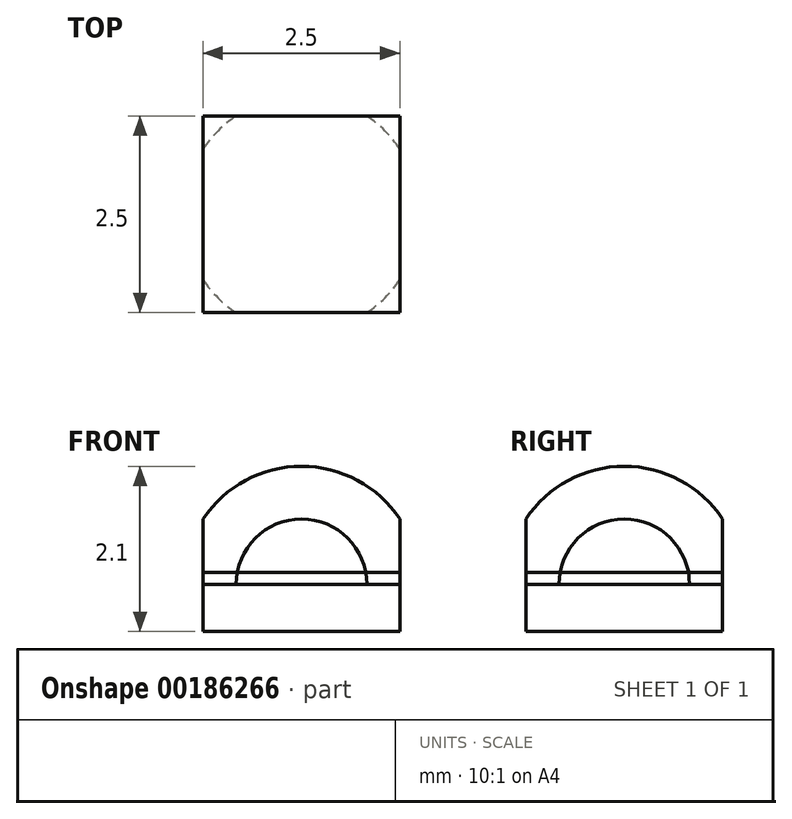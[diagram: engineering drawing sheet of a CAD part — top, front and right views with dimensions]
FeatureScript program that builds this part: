
annotation { "Feature Type Name" : "Feature", "Feature Type Description" : "" }
export const myFeature = defineFeature(function(context is Context, id is Id, definition is map)
    precondition{}
    {
        {
            var Q0;
            Q0=qCreatedBy(makeId("Top.planeOp"),FACE);
            var sketch = newSketch(context, id + "F0", { "sketchPlane" : qUnion([Q0])});
            skLineSegment(sketch, "E0.bottom", {"start": v(1.25, 1.25) * mm, "end": v(-1.25, 1.25) * mm});
            skLineSegment(sketch, "E0.top", {"start": v(1.25, -1.25) * mm, "end": v(-1.25, -1.25) * mm});
            skLineSegment(sketch, "E0.left", {"start": v(1.25, 1.25) * mm, "end": v(1.25, -1.25) * mm});
            skLineSegment(sketch, "E0.right", {"start": v(-1.25, 1.25) * mm, "end": v(-1.25, -1.25) * mm});
            skPoint(sketch, "E0.middle", {"position": v(0, 0) * mm});
            skSolve(sketch);
        }
        {
            var Q0;
            Q0 = qSketchRegion(id + "F0", true);
            extrude(context, id + "F1", {"entities" : qUnion([Q0]), "depth" : .6 * mm});
        }
        {
            var Q0;
            Q0=makeQuery(id+"F1.opExtrude","CAP_FACE",FACE,{"disambiguationData":[OSD([sQuery(id+"F0.wireOp",EDGE,"E0.bottom"),sQuery(id+"F0.wireOp",EDGE,"E0.top"),sQuery(id+"F0.wireOp",EDGE,"E0.left"),sQuery(id+"F0.wireOp",EDGE,"E0.right")])],"isStart":false});
            var sketch = newSketch(context, id + "F2", { "sketchPlane" : qUnion([Q0])});
            skLineSegment(sketch, "E1.bottom", {"start": v(-1.25, -1.25) * mm, "end": v(1.25, -1.25) * mm});
            skLineSegment(sketch, "E1.top", {"start": v(-1.25, 1.25) * mm, "end": v(1.25, 1.25) * mm});
            skLineSegment(sketch, "E1.left", {"start": v(-1.25, -1.25) * mm, "end": v(-1.25, 1.25) * mm});
            skLineSegment(sketch, "E1.right", {"start": v(1.25, -1.25) * mm, "end": v(1.25, 1.25) * mm});
            skSolve(sketch);
        }
        {
            var Q0;
            Q0 = qSketchRegion(id + "F2", true);
            extrude(context, id + "F3", {"entities" : qUnion([Q0]), "depth" : .15 * mm});
        }
        {
            var Q0;
            Q0=qCreatedBy(makeId("Front.planeOp"),FACE);
            var sketch = newSketch(context, id + "F4", { "sketchPlane" : qUnion([Q0])});
            skLineSegment(sketch, "E2", {"start": v(0, 0) * mm, "end": v(0, 2.47) * mm, "construction": true});
            skSolve(sketch);
        }
        {
            var Q0;
            Q0=qCreatedBy(makeId("Front.planeOp"),FACE);
            var sketch = newSketch(context, id + "F5", { "sketchPlane" : qUnion([Q0])});
            skArc(sketch, "E3", {"start": v(1.5, 0.6) * mm, "mid": v(0, 2.1) * mm, "end": v(-1.5, 0.6) * mm});
            skPoint(sketch, "E4", {"position": v(0, 2.1) * mm});
            skLineSegment(sketch, "E5", {"start": v(-1.5, 0.6) * mm, "end": v(1.5, 0.6) * mm});
            skSolve(sketch);
        }
        {
            var Q0;
            Q0=makeQuery(id+"F5.imprint","IMPRINT",FACE,{"disambiguationData":[TD([[makeQuery(id+"F5.imprint","IMPRINT",EDGE,{"derivedFrom":sQuery(id+"F5.wireOp",EDGE,"E3")}),1.0]])]});
            var Q1;
            Q1=sQuery(id+"F5.wireOp",EDGE,"E5");
            revolve(context, id + "F6", {"entities" : qUnion([Q0]), "axis" : qUnion([Q1]), "revolveType" : RevolveType.SYMMETRIC, "angle" : 180 * degree});
        }
        {
            var Q0;
            Q0=makeQuery(id+"F1.opExtrude","CAP_FACE",FACE,{"disambiguationData":[OSD([sQuery(id+"F0.wireOp",EDGE,"E0.bottom"),sQuery(id+"F0.wireOp",EDGE,"E0.top"),sQuery(id+"F0.wireOp",EDGE,"E0.left"),sQuery(id+"F0.wireOp",EDGE,"E0.right")])],"isStart":true});
            var sketch = newSketch(context, id + "F7", { "sketchPlane" : qUnion([Q0])});
            skLineSegment(sketch, "E6.bottom", {"start": v(-1.25, -1.25) * mm, "end": v(1.25, -1.25) * mm});
            skLineSegment(sketch, "E6.top", {"start": v(-1.25, 1.25) * mm, "end": v(1.25, 1.25) * mm});
            skLineSegment(sketch, "E6.left", {"start": v(-1.25, -1.25) * mm, "end": v(-1.25, 1.25) * mm});
            skLineSegment(sketch, "E6.right", {"start": v(1.25, -1.25) * mm, "end": v(1.25, 1.25) * mm});
            skSolve(sketch);
        }
        {
            var Q0;
            Q0 = qSketchRegion(id + "F7", true);
            extrude(context, id + "F8", {"entities" : qUnion([Q0]), "operationType" : NewBodyOperationType.INTERSECT, "endBound" : BoundingType.THROUGH_ALL, "oppositeDirection" : true, "depth" : 25 * mm});
        }
    });
